# Revit family: Shower-Handshower-KOHLER-Flipside-K-17493BR_1
name_source: partatom
category: Plumbing Fixtures
units: mm (PartAtom-declared; Revit-internal decimal feet)

## family parameters
Cut with Voids When Loaded = No
Host = Face
OmniClass Number = 23.31.17.00
OmniClass Title = Showers
Part Type = Normal
Room Calculation Point = No
Round Connector Dimension = Use Diameter
Shared = No

## types (1)
- CP-Polished Chrome
    ADA Compliant = No
    Assembly Code = D2010700
    CW Connection = No
    Cold Water Inlet = Cold Water Inlet
    Date Modified = 09/22/2022
    Default Elevation = 0"
    Description = MULTI FUNCTION HANDSHOWER
    Drain Included = No
    Finish = Kohler-Plastic-CP-Polished_Chrome
    Flow Rate = 3 GPM
    HW Connection = Yes
    Height = 11"
    Hot Water Inlet = Hot Water Inlet
    Length = 4 1/16"
    Manufacturer = Kohler Co.
    Master Format 2014 = 22 42 23
    Master Format 2014 Name = Residential Showers
    Material = Plastic
    Model = K-17493BR
    Panel Thickness = 0"
    Pressure = 80.00 psi
    Product Name = Flipside
    Tempered Water Inlet = Tempered Water Inlet
    Type = 1
    URL = https://br.kohler.com
    Vent Connection = No
    Waste Connection = No
    Waste Water Outlet = Waste Water Outlet
    WaterSense Certified = No
    Width = 5 3/8"

## geometry (parser evidence)
native form markers: Sweep x4
no freeform markers — native parametric forms only
